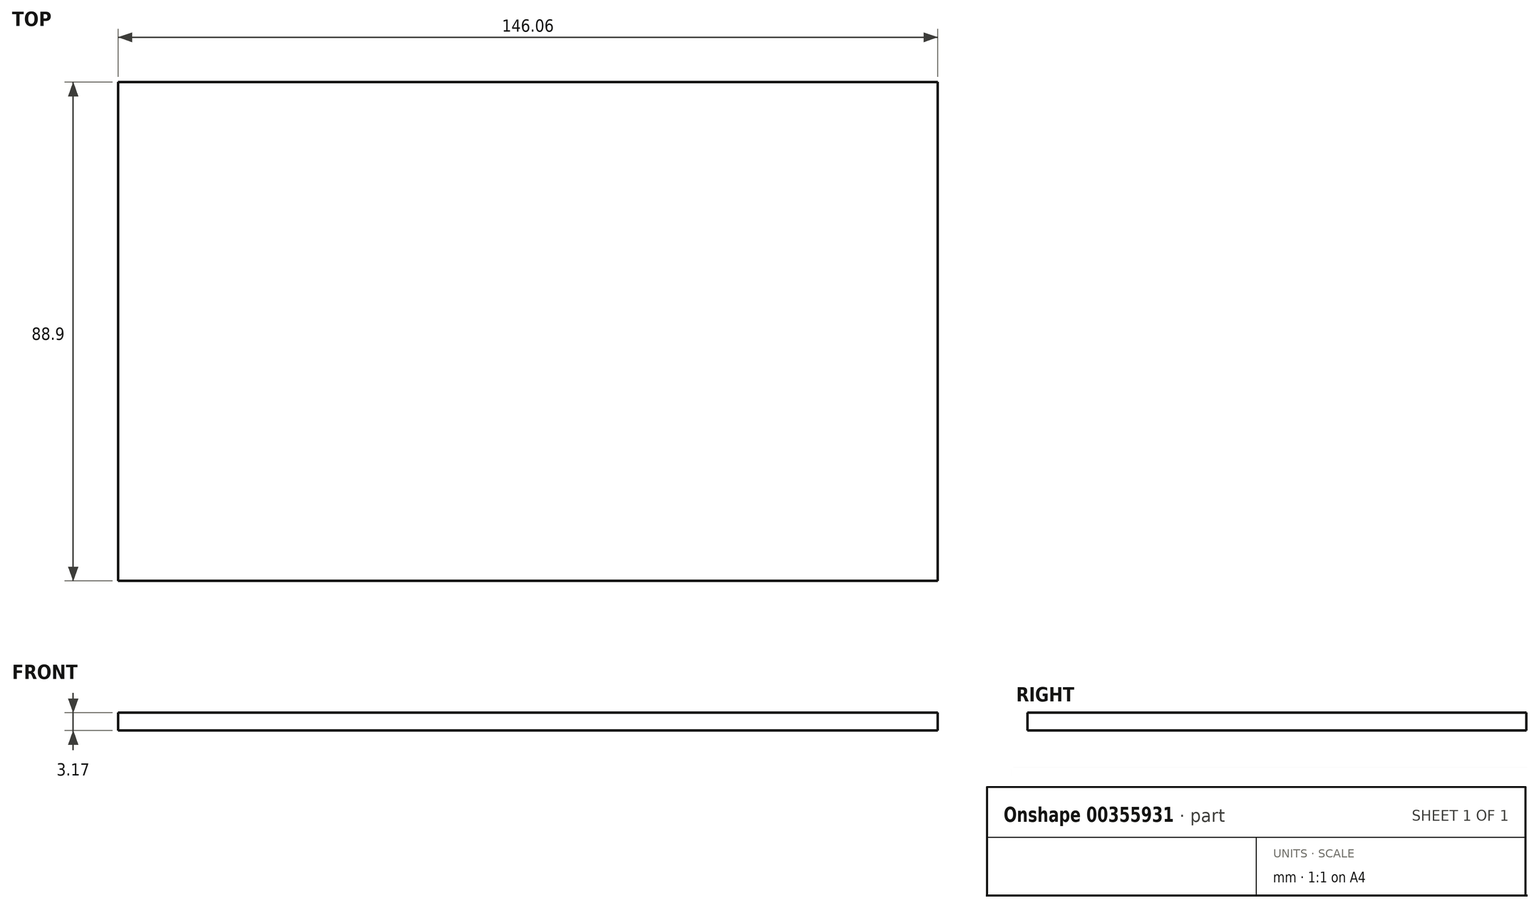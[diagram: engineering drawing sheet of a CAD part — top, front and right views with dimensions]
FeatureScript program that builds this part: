
annotation { "Feature Type Name" : "Feature", "Feature Type Description" : "" }
export const myFeature = defineFeature(function(context is Context, id is Id, definition is map)
    precondition{}
    {
        {
            var Q0;
            Q0=qCreatedBy(makeId("Top.planeOp"),FACE);
            var sketch = newSketch(context, id + "F0", { "sketchPlane" : qUnion([Q0])});
            skLineSegment(sketch, "E0.bottom", {"start": v(73.03, -44.45) * mm, "end": v(-73.03, -44.45) * mm});
            skLineSegment(sketch, "E0.top", {"start": v(73.03, 44.45) * mm, "end": v(-73.03, 44.45) * mm});
            skLineSegment(sketch, "E0.left", {"start": v(73.03, -44.45) * mm, "end": v(73.03, 44.45) * mm});
            skLineSegment(sketch, "E0.right", {"start": v(-73.03, -44.45) * mm, "end": v(-73.03, 44.45) * mm});
            skPoint(sketch, "E0.middle", {"position": v(0, 0) * mm});
            skSolve(sketch);
        }
        {
            var Q0;
            Q0=makeQuery(id+"F0.imprint","IMPRINT",FACE,{"disambiguationData":[TD([[makeQuery(id+"F0.imprint","IMPRINT",EDGE,{"derivedFrom":sQuery(id+"F0.wireOp",EDGE,"E0.bottom")}),-1.0]])]});
            extrude(context, id + "F1", {"entities" : qUnion([Q0]), "depth" : 3.17 * mm});
        }
    });
